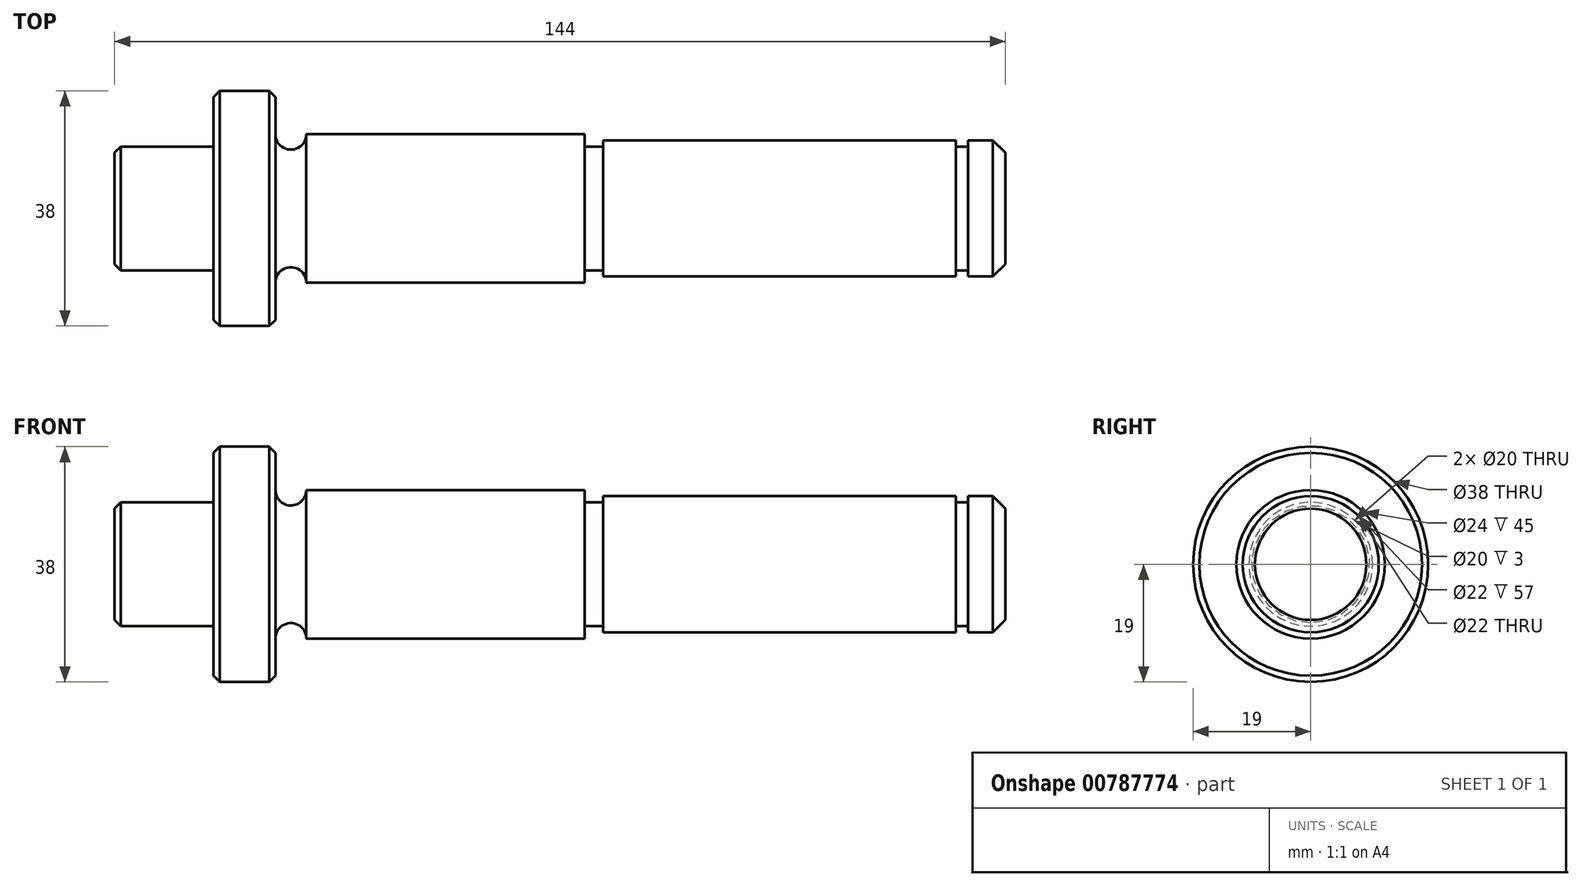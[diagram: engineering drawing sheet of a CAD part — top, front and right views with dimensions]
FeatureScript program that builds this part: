
annotation { "Feature Type Name" : "Feature", "Feature Type Description" : "" }
export const myFeature = defineFeature(function(context is Context, id is Id, definition is map)
    precondition{}
    {
        {
            var Q0;
            Q0=qCreatedBy(makeId("Front.planeOp"),FACE);
            var sketch = newSketch(context, id + "F0", { "sketchPlane" : qUnion([Q0])});
            skLineSegment(sketch, "E0", {"start": v(0, 0) * mm, "end": v(144, 0) * mm});
            skLineSegment(sketch, "E1", {"start": v(0, 0) * mm, "end": v(0, 10) * mm});
            skLineSegment(sketch, "E2", {"start": v(0, 10) * mm, "end": v(16, 10) * mm});
            skLineSegment(sketch, "E3", {"start": v(16, 10) * mm, "end": v(16, 19) * mm});
            skLineSegment(sketch, "E4", {"start": v(16, 19) * mm, "end": v(26, 19) * mm});
            skLineSegment(sketch, "E5", {"start": v(26, 19) * mm, "end": v(26, 12) * mm});
            skLineSegment(sketch, "E6", {"start": v(76, 12) * mm, "end": v(76, 10) * mm});
            skLineSegment(sketch, "E7", {"start": v(76, 10) * mm, "end": v(79, 10) * mm});
            skLineSegment(sketch, "E8", {"start": v(79, 10) * mm, "end": v(79, 11) * mm});
            skLineSegment(sketch, "E9", {"start": v(79, 11) * mm, "end": v(136, 11) * mm});
            skLineSegment(sketch, "E10", {"start": v(136, 11) * mm, "end": v(136, 10) * mm});
            skLineSegment(sketch, "E11", {"start": v(136, 10) * mm, "end": v(138, 10) * mm});
            skLineSegment(sketch, "E12", {"start": v(138, 10) * mm, "end": v(138, 11) * mm});
            skLineSegment(sketch, "E13", {"start": v(138, 11) * mm, "end": v(144, 11) * mm});
            skLineSegment(sketch, "E14", {"start": v(144, 11) * mm, "end": v(144, 0) * mm});
            skArc(sketch, "E15", {"start": v(26, 12) * mm, "mid": v(28.5, 9.5) * mm, "end": v(31, 12) * mm});
            skLineSegment(sketch, "E16", {"start": v(31, 12) * mm, "end": v(76, 12) * mm});
            skSolve(sketch);
        }
        {
            var Q0;
            Q0=sQuery(id+"F0.wireOp",EDGE,"E1");
            var Q1;
            Q1=sQuery(id+"F0.wireOp",EDGE,"E2");
            var Q2;
            Q2=sQuery(id+"F0.wireOp",EDGE,"E4");
            var Q3;
            Q3=sQuery(id+"F0.wireOp",EDGE,"E3");
            var Q4;
            Q4=sQuery(id+"F0.wireOp",EDGE,"E5");
            var Q5;
            Q5=sQuery(id+"F0.wireOp",EDGE,"E15");
            var Q6;
            Q6=sQuery(id+"F0.wireOp",EDGE,"E16");
            var Q7;
            Q7=sQuery(id+"F0.wireOp",EDGE,"E6");
            var Q8;
            Q8=sQuery(id+"F0.wireOp",EDGE,"E7");
            var Q9;
            Q9=sQuery(id+"F0.wireOp",EDGE,"E8");
            var Q10;
            Q10=sQuery(id+"F0.wireOp",EDGE,"E9");
            var Q11;
            Q11=sQuery(id+"F0.wireOp",EDGE,"E14");
            var Q12;
            Q12=sQuery(id+"F0.wireOp",EDGE,"E13");
            var Q13;
            Q13=sQuery(id+"F0.wireOp",EDGE,"E11");
            var Q14;
            Q14=sQuery(id+"F0.wireOp",EDGE,"E0");
            revolve(context, id + "F1", {"bodyType" : ToolBodyType.SURFACE, "surfaceOperationType" : NewSurfaceOperationType.NEW, "surfaceEntities" : qUnion([Q0, Q1, Q2, Q3, Q4, Q5, Q6, Q7, Q8, Q9, Q10, Q11, Q12, Q13]), "axis" : qUnion([Q14]), "revolveType" : RevolveType.FULL});
        }
        {
            var Q0;
            Q0=makeQuery(id+"F1.opRevolve","SWEPT_EDGE",EDGE,{"disambiguationData":[OSD([sQuery(id+"F0.wireOp",VERTEX,"E5.start")])]});
            var Q1;
            Q1=makeQuery(id+"F1.opRevolve","SWEPT_EDGE",EDGE,{"disambiguationData":[OSD([sQuery(id+"F0.wireOp",VERTEX,"E3.end")])]});
            var Q2;
            Q2=makeQuery(id+"F1.opRevolve","SWEPT_EDGE",EDGE,{"disambiguationData":[OSD([sQuery(id+"F0.wireOp",VERTEX,"E2.start")])]});
            chamfer(context, id + "F2", {"entities" : qUnion([Q0, Q1, Q2]), "width" : 1 * mm, "tangentPropagation" : true});
        }
        {
            var Q0;
            Q0=makeQuery(id+"F1.opRevolve","SWEPT_EDGE",EDGE,{"disambiguationData":[OSD([sQuery(id+"F0.wireOp",VERTEX,"E13.end")])]});
            chamfer(context, id + "F3", {"entities" : qUnion([Q0]), "width" : 2 * mm, "tangentPropagation" : true});
        }
    });
